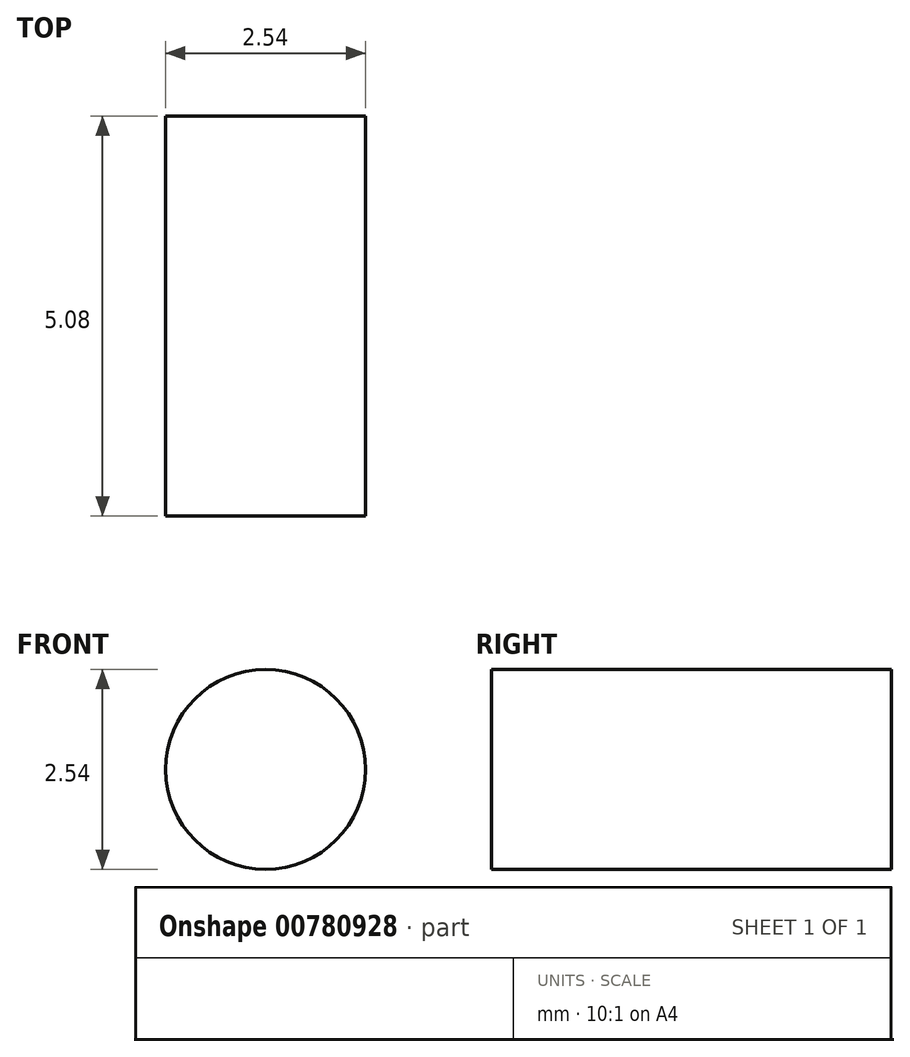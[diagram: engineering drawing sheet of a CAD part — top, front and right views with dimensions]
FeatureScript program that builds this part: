
annotation { "Feature Type Name" : "Feature", "Feature Type Description" : "" }
export const myFeature = defineFeature(function(context is Context, id is Id, definition is map)
    precondition{}
    {
        {
            var Q0;
            Q0=qCreatedBy(makeId("Front.planeOp"),FACE);
            var sketch = newSketch(context, id + "F0", { "sketchPlane" : qUnion([Q0])});
            skCircle(sketch, "E0", {"center": v(0, 0) * mm, "radius": 1.27 * mm});
            skSolve(sketch);
        }
        {
            var Q0;
            Q0 = qSketchRegion(id + "F0", true);
            extrude(context, id + "F1", {"entities" : qUnion([Q0]), "depth" : 5.08 * mm, "offsetDistance" : 25.4 * mm});
        }
    });
